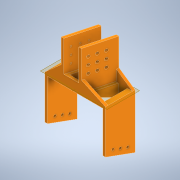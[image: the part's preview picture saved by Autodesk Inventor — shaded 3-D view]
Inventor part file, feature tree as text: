
AUTODESK INVENTOR PART (.ipt)
format: ipt  version: 2022.1 (Build 261234020, 234B)  size: 369,664 bytes
history: native  units: mm
features: sketch x20, extrude x9, loft x4, hole x3, projected_geometry x1
ambient origin geometry x8: Origin, YZ Plane, XZ Plane, XY Plane, X Axis, Y Axis, Z Axis, Center Point
bodies: Body1 (feature_tree)
feature tree (37):
  extrude  "Extrusion8"  Depth=164.0mm
  extrude  "armsForCameraCase"  TaperAngle=0.0deg  [1 undecoded]
  extrude  "Extrusion10"  Depth=7.0mm
  extrude  "Extrusion11"  Depth=125.0mm TaperAngle=0.0deg
  extrude  "Extrusion12"  Depth=7.0mm
  hole  "Hole1"  [1 undecoded]
  extrude  "Extrusion13"  Depth=104.1375mm
  hole  "HoleForLeftSideOf2x4"  [1 undecoded]
  hole  "HolesForRightSideOf2x4"  [1 undecoded]
  extrude  "Extrusion14"  TaperAngle=0.0deg  [1 undecoded]
  extrude  "Extrusion15"  Depth=21.283555mm
  extrude  "Extrusion16"  Depth=30.0mm
  loft  "Loft5"
  loft  "Loft6"
  loft  "Loft7"
  loft  "Loft8"
  sketch  "Sketch8"  dims[d28=80.0mm d29=164.0mm]
  sketch  "Sketch9"  dims[d30=7.0mm d31=0.0mm]
  sketch  "Sketch10"  dims[d32=7.0mm d33=7.0mm]
  sketch  "Sketch11"  dims[d34=140.0mm d35=0.0mm d37=125.0mm d38=0.0mm]
  sketch  "Sketch12"  dims[d39=-2.617994mm d40=7.0mm]
  sketch  "Sketch13"  dims[d42=7.0mm d44=20.32mm]
  sketch  "Sketch14"  dims[d45=20.32mm d46=104.1375mm]
  sketch  "Sketch15"  dims[d47=0.0mm d48=3.490659mm]
  sketch  "Sketch16"  dims[d49=20.0mm d50=0.0mm d51=90.0mm]
  sketch  "Sketch17"  dims[d52=6.7564mm d53=6.0mm d54=15.875mm d55=4.826mm d56=14.3117mm d57=8.0mm d58=20.594885mm d59=0.0mm d60=0.0mm]
  sketch  "Sketch18"  dims[d62=21.283555mm d63=21.283555mm]
  projected_geometry  "Projected Loop3"
  sketch  "Sketch19"  dims[d64=25.0mm]
  sketch  "Sketch27"  dims[d65=4.496mm d66=6.0mm d67=8.433mm d68=2.794mm d69=14.3117mm d70=8.0mm d71=0.0mm d72=30.0mm d74=20.0mm d75=30.0mm d77=20.0mm]
  sketch  "Sketch28"  dims[d80=20.0mm d81=15.0mm]
  sketch  "Sketch29"  dims[d82=30.0mm d84=20.0mm d85=30.0mm d87=20.0mm d90=20.0mm]
  sketch  "Sketch30"  dims[d91=4.496mm d92=6.0mm d93=8.433mm d94=2.0mm d95=14.3117mm d96=8.0mm d97=0.0mm d98=7.0mm]
  sketch  "Sketch31"  dims[d99=7.0mm d101=7.0mm]
  sketch  "Sketch32"  dims[d102=7.0mm]
  sketch  "Sketch33"  dims[d103=0.0mm d104=0.0mm]
  sketch  "Sketch34"  dims[d105=7.0mm d107=7.0mm d108=14.0mm d109=7.0mm d110=0.0mm d111=0.0mm d112=7.0mm d113=14.0mm d114=7.0mm d115=7.0mm d116=0.0mm d117=0.0mm d152=30.0mm d153=30.0mm d154=0.0mm d155=90.0deg d156=0.0mm d157=90.0deg d158=30.0mm d159=30.0mm d160=0.0mm d161=90.0deg d162=0.0mm d163=90.0deg d164=39.0mm d165=30.0mm d166=0.0mm d167=90.0deg d168=0.0mm d169=90.0deg d170=30.0mm d171=30.0mm d172=0.0mm d173=90.0deg d174=0.0mm d175=90.0deg d73=0.0625mm]
note: 5 required parameter values undecoded (feature->parameter linkage not recoverable at this tier; creation-order binding heuristic only, values carry confidence <= 0.55)
